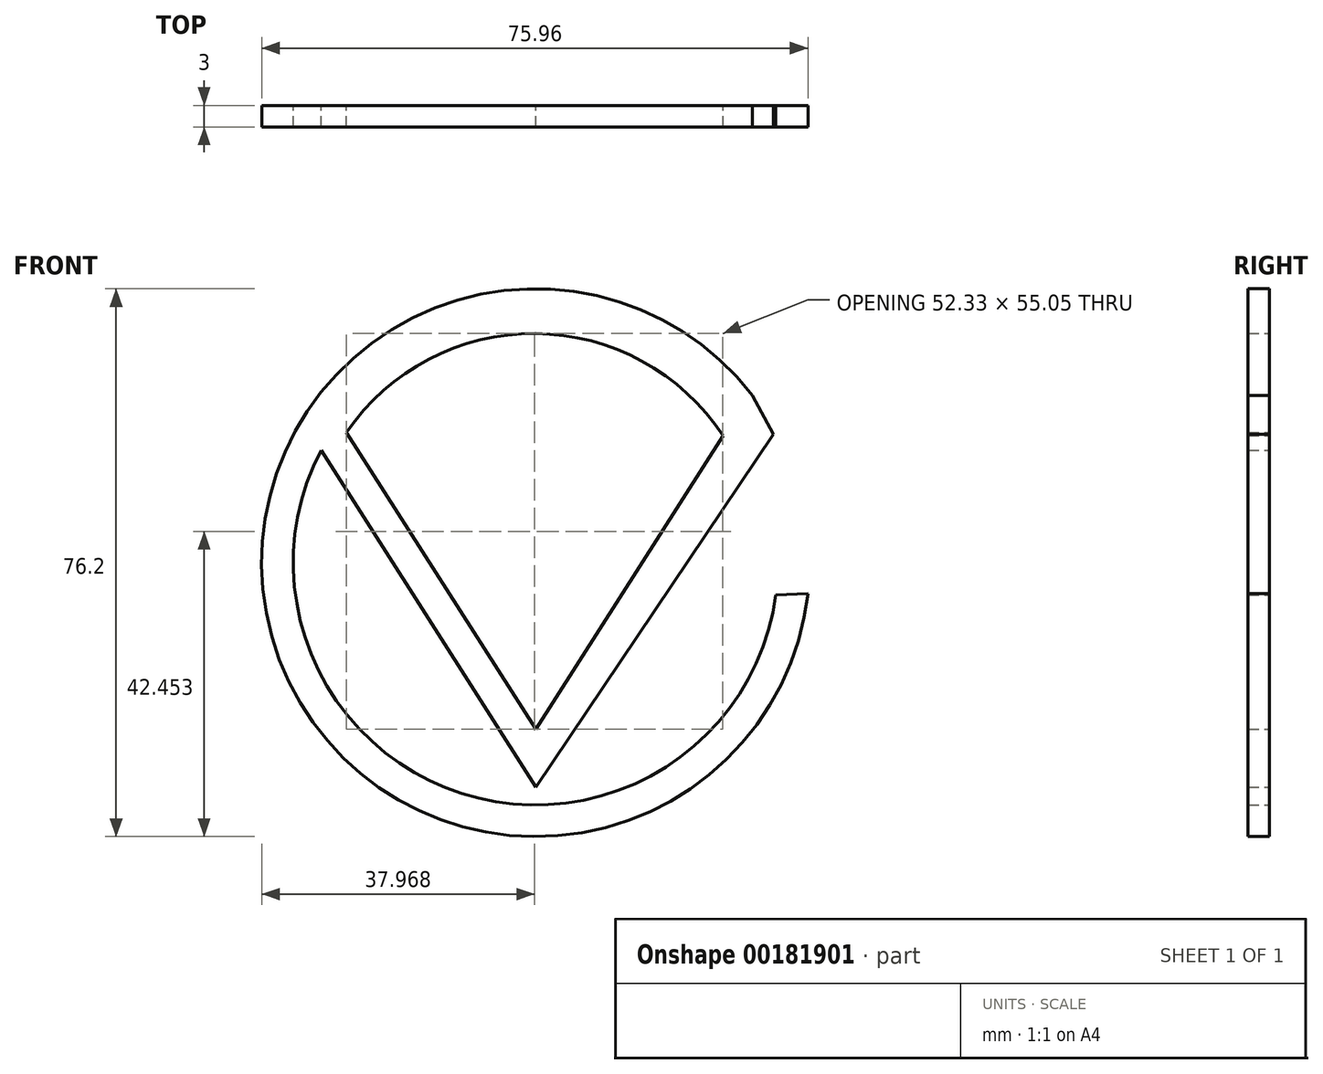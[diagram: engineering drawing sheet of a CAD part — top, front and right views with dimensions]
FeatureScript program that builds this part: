
annotation { "Feature Type Name" : "Feature", "Feature Type Description" : "" }
export const myFeature = defineFeature(function(context is Context, id is Id, definition is map)
    precondition{}
    {
        {
            var Q0;
            Q0=qCreatedBy(makeId("Front.planeOp"),FACE);
            var sketch = newSketch(context, id + "F0", { "sketchPlane" : qUnion([Q0])});
            skLineSegment(sketch, "E0", {"start": v(-26.3, 18.12) * mm, "end": v(0, -23.17) * mm});
            skLineSegment(sketch, "E1", {"start": v(0, -23.17) * mm, "end": v(26.03, 17.66) * mm});
            skArc(sketch, "E2", {"start": v(30.15, 23.3) * mm, "mid": v(-36.7, -10.27) * mm, "end": v(37.86, -4.26) * mm});
            skLineSegment(sketch, "E3", {"start": v(33.05, 17.88) * mm, "end": v(30.15, 23.3) * mm});
            skArc(sketch, "E4.trimOffspring", {"start": v(-28.44, 18.08) * mm, "mid": v(-28.46, 18.04) * mm, "end": v(-28.48, 18) * mm});
            skArc(sketch, "E5", {"start": v(26.03, 17.66) * mm, "mid": v(0, 31.88) * mm, "end": v(-26.3, 18.12) * mm});
            skLineSegment(sketch, "E6", {"start": v(0, -31.2) * mm, "end": v(-29.84, 15.65) * mm});
            skLineSegment(sketch, "E7", {"start": v(0, -31.2) * mm, "end": v(33.05, 17.88) * mm});
            skLineSegment(sketch, "E8", {"start": v(-29.84, 15.65) * mm, "end": v(-29.84, 15.65) * mm});
            skArc(sketch, "E9", {"start": v(-29.44, 16.39) * mm, "mid": v(-29.64, 16.02) * mm, "end": v(-29.84, 15.65) * mm});
            skArc(sketch, "E10", {"start": v(-29.84, 15.65) * mm, "mid": v(-10.3, -32.08) * mm, "end": v(33.38, -4.64) * mm});
            skArc(sketch, "E11", {"start": v(-29.84, 15.65) * mm, "mid": v(-10.24, -32.1) * mm, "end": v(33.4, -4.5) * mm});
            skLineSegment(sketch, "E12", {"start": v(33.4, -4.5) * mm, "end": v(37.86, -4.26) * mm});
            skSolve(sketch);
        }
        {
            var Q0;
            Q0 = qSketchRegion(id + "F0", true);
            extrude(context, id + "F1", {"entities" : qUnion([Q0]), "depth" : 3 * mm});
        }
    });
